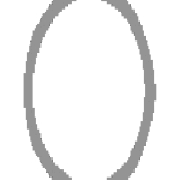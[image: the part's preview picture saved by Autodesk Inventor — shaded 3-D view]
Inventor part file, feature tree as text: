
AUTODESK INVENTOR PART (.ipt)
format: ipt  version: 2021 (Build 250183000, 183)  size: 109,568 bytes
history: native  units: in
note: dims shown in document units (in); Inventor stores cm internally (conversion verified against a paired STEP export)
features: other x4, sketch x3, plane x1
ambient origin geometry x8: Origin, YZ Plane, XZ Plane, XY Plane, X Axis, Y Axis, Z Axis, Center Point
bodies: Solid1 (feature_tree), Body (feature_tree)
feature tree (8):
  other  "Driven Length"
  other  "Frame Generator"
  other  "Start Plane"
  other  "End Plane"
  sketch  "Sketch"  dims[d2=32.7942in d4=-0.0in d5=32.7942in d6=0.12in d7=0.0in d8=90.0deg d9=32.7942in]
  sketch  "Sketch2"  dims[d0=1.0in]
  plane  "Work Plane3"
  sketch  "Sketch3"  dims[d1=0.065in]
